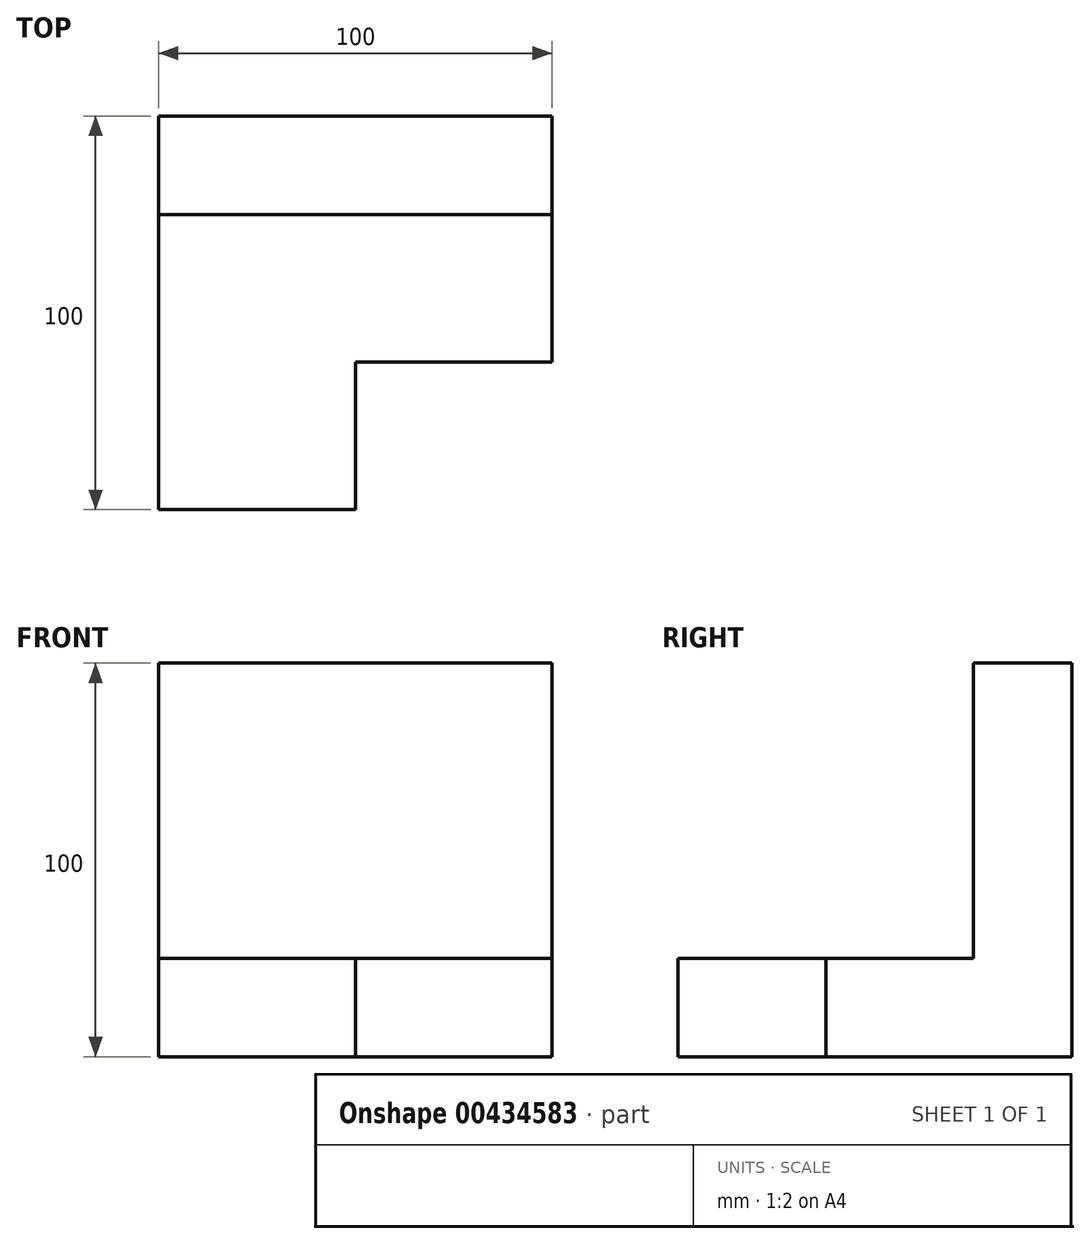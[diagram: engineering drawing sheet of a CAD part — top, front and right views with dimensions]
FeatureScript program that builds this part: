
annotation { "Feature Type Name" : "Feature", "Feature Type Description" : "" }
export const myFeature = defineFeature(function(context is Context, id is Id, definition is map)
    precondition{}
    {
        {
            var Q0;
            Q0=qCreatedBy(makeId("Top.planeOp"),FACE);
            var sketch = newSketch(context, id + "F0", { "sketchPlane" : qUnion([Q0])});
            skLineSegment(sketch, "E0.bottom", {"start": v(0, 0) * mm, "end": v(-100, 0) * mm});
            skLineSegment(sketch, "E0.top", {"start": v(0, 100) * mm, "end": v(-100, 100) * mm});
            skLineSegment(sketch, "E0.left", {"start": v(0, 0) * mm, "end": v(0, 100) * mm});
            skLineSegment(sketch, "E0.right", {"start": v(-100, 0) * mm, "end": v(-100, 100) * mm});
            skSolve(sketch);
        }
        {
            var Q0;
            Q0=makeQuery(id+"F0.imprint","IMPRINT",FACE,{"disambiguationData":[TD([[makeQuery(id+"F0.imprint","IMPRINT",EDGE,{"derivedFrom":sQuery(id+"F0.wireOp",EDGE,"E0.bottom")}),-1.0]])]});
            extrude(context, id + "F1", {"entities" : qUnion([Q0]), "oppositeDirection" : true, "depth" : 100 * mm});
        }
        {
            var Q0;
            Q0=makeQuery(id+"F1.opExtrude","CAP_FACE",FACE,{"disambiguationData":[OSD([sQuery(id+"F0.wireOp",EDGE,"E0.bottom"),sQuery(id+"F0.wireOp",EDGE,"E0.top"),sQuery(id+"F0.wireOp",EDGE,"E0.left"),sQuery(id+"F0.wireOp",EDGE,"E0.right")])],"isStart":true});
            var sketch = newSketch(context, id + "F2", { "sketchPlane" : qUnion([Q0])});
            skLineSegment(sketch, "E1.bottom", {"start": v(-100, 0) * mm, "end": v(0, 0) * mm});
            skLineSegment(sketch, "E1.top", {"start": v(-100, 75) * mm, "end": v(0, 75) * mm});
            skLineSegment(sketch, "E1.left", {"start": v(-100, 0) * mm, "end": v(-100, 75) * mm});
            skLineSegment(sketch, "E1.right", {"start": v(0, 0) * mm, "end": v(0, 75) * mm});
            skSolve(sketch);
        }
        {
            var Q0;
            Q0=makeQuery(id+"F2.imprint","IMPRINT",FACE,{"disambiguationData":[TD([[makeQuery(id+"F2.imprint","IMPRINT",EDGE,{"derivedFrom":sQuery(id+"F2.wireOp",EDGE,"E1.bottom")}),-1.0]])]});
            extrude(context, id + "F3", {"entities" : qUnion([Q0]), "operationType" : NewBodyOperationType.REMOVE, "oppositeDirection" : true, "depth" : 75 * mm});
        }
        {
            var Q0;
            Q0=makeQuery(id+"F3.boolean.opBoolean","COPY",FACE,{"derivedFrom":makeQuery(id+"F3.opExtrude","CAP_FACE",FACE,{"disambiguationData":[OSD([sQuery(id+"F2.wireOp",EDGE,"E1.bottom"),sQuery(id+"F2.wireOp",EDGE,"E1.top"),sQuery(id+"F2.wireOp",EDGE,"E1.left"),sQuery(id+"F2.wireOp",EDGE,"E1.right")])],"isStart":false})});
            var sketch = newSketch(context, id + "F4", { "sketchPlane" : qUnion([Q0])});
            skPoint(sketch, "E2.oppositeSnap0", {"position": v(-50, 75) * mm});
            skPoint(sketch, "E2.oppositeSnap1", {"position": v(-100, 37.5) * mm});
            skLineSegment(sketch, "E2.bottom", {"start": v(0, 0) * mm, "end": v(-50, 0) * mm});
            skLineSegment(sketch, "E2.top", {"start": v(0, 37.5) * mm, "end": v(-50, 37.5) * mm});
            skLineSegment(sketch, "E2.left", {"start": v(0, 0) * mm, "end": v(0, 37.5) * mm});
            skLineSegment(sketch, "E2.right", {"start": v(-50, 0) * mm, "end": v(-50, 37.5) * mm});
            skSolve(sketch);
        }
        {
            var Q0;
            Q0=makeQuery(id+"F4.imprint","IMPRINT",FACE,{"disambiguationData":[TD([[makeQuery(id+"F4.imprint","IMPRINT",EDGE,{"derivedFrom":sQuery(id+"F4.wireOp",EDGE,"E2.bottom")}),-1.0]])]});
            extrude(context, id + "F5", {"entities" : qUnion([Q0]), "operationType" : NewBodyOperationType.REMOVE, "endBound" : BoundingType.THROUGH_ALL, "oppositeDirection" : true, "depth" : 81 * mm});
        }
    });
